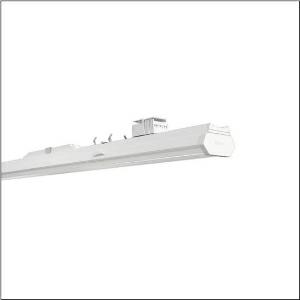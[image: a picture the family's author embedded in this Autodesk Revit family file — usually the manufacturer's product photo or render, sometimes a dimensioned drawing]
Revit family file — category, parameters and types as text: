
# Revit family: licross_r__11_protected_ho_51tp11cn4dxr_68be
name_source: partatom
category: Lighting Fixtures
units: mm (PartAtom-declared; Revit-internal decimal feet)

## family parameters
Cut with Voids When Loaded = No
Host = Face
Light Source = No
Part Type = Normal
Room Calculation Point = No
Round Connector Dimension = Use Diameter
Shared = No

## types (1)
- --- (1 x LED, 13240 lm, 76.4 W, 4000K)
    Apparent Load = 76 VA
    CIE Flux Codes = 84 94 98 99 100
    Color Rendering = 80
    Color Temperature = 4000K
    Default Elevation = 1800 mm
    Description = Licross® 11 Protected HOluminaire insert, length: 1.500mm, width: 90mm, height: 101mm, LED rated luminous flux: 13.240lm, light colour: 840, control gear: ON/OFF Multilumen, CLOi, control gear: ECG Multilumen, with plug, 3-pole, with phase selection, mains connection: 220..240V, AC, 50/60Hz, halogen-free wiring, primary optical cover: cover, of PMMA, light emission: direct with ceiling illumination distribution, protection rating (complete): IP64, insulation class (complete): insulation class I (protective earthing), certification: CE, ENEC, VDE, protection symbol: D if used in an environment with conductive dust loads with corresponding accessories, permissible ambient temperature for indoor applications: -35..+40°C, reducing of maximum allowable ambient temperature of 5°C with ceiling mounting, corresponds to IFS (International Featured Standards) requirements for safety and quality in the food industry, packaging unit: 1 piece
    Height = 92 mm
    Lamp = 1 x LED
    Lamp Light Flux = 13240 lm
    Lamp Power = 76.4 W
    Lamp count = 1
    Length = 1500 mm
    Luminous efficacy = 173 lm/W
    Manufacturer = Siteco
    ModVariant = No
    Model = 51TP11CN4DXR
    Mounting Place = Ceiling
    Mounting Type = Pendant
    Number of Poles = 1
    OnlyDefault = Yes
    Power Factor = 1
    Product Name = Licross® 11 Protected HO
    Product group = luminaire insert
    ProductGroupID = 902
    Protection Class = Protection class I
    Protection Degree = IP 64
    RLX_Detail_Level = 1
    RlxData = <blob elided: 21693 chars, md5=fe7e26af>
    Socket = socket
    Standby Power = 0 W
    System Light Flux = 13240 lm
    System Power = 76 W
    Type Comments = factory setting: luminous flux: 100 % | (A | C | E) | 177 mA
    Type Image = l_1256148.jpg
    URL = http://relux.com
    VarID = @adj_137773
    Voltage = 0 V
    Weight = 0.00 kg
    Width = 88 mm

## geometry (parser evidence)
native form markers: Blend x4, Sweep x10
no freeform markers — native parametric forms only
